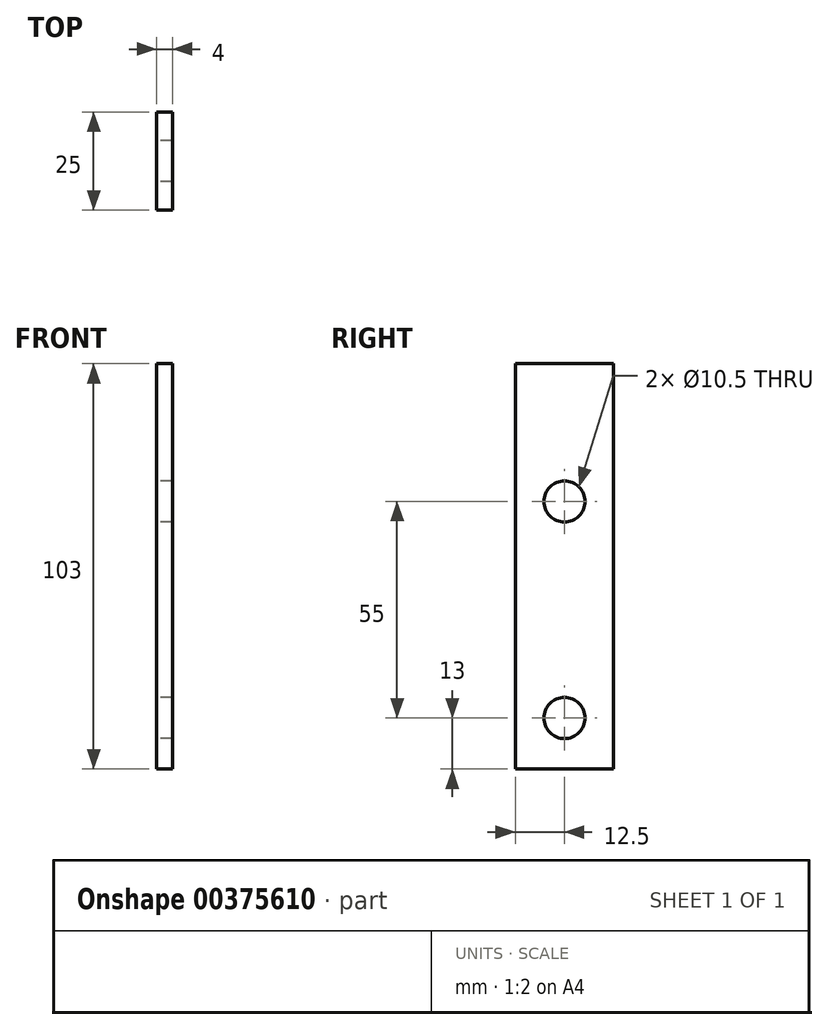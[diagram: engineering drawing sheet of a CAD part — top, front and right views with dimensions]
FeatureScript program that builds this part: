
annotation { "Feature Type Name" : "Feature", "Feature Type Description" : "" }
export const myFeature = defineFeature(function(context is Context, id is Id, definition is map)
    precondition{}
    {
        {
            var Q0;
            Q0=qCreatedBy(makeId("Right.planeOp"),FACE);
            var sketch = newSketch(context, id + "F0", { "sketchPlane" : qUnion([Q0])});
            skLineSegment(sketch, "E0.bottom", {"start": v(12.5, 51.5) * mm, "end": v(-12.5, 51.5) * mm});
            skLineSegment(sketch, "E0.top", {"start": v(12.5, -51.5) * mm, "end": v(-12.5, -51.5) * mm});
            skLineSegment(sketch, "E0.left", {"start": v(12.5, 51.5) * mm, "end": v(12.5, -51.5) * mm});
            skLineSegment(sketch, "E0.right", {"start": v(-12.5, 51.5) * mm, "end": v(-12.5, -51.5) * mm});
            skPoint(sketch, "E0.middle", {"position": v(0, 0) * mm});
            skLineSegment(sketch, "E1.bottom", {"start": v(98.77, -18.5) * mm, "end": v(-98.77, -18.5) * mm, "construction": true});
            skLineSegment(sketch, "E1.top", {"start": v(98.77, -98.5) * mm, "end": v(-98.77, -98.5) * mm, "construction": true});
            skLineSegment(sketch, "E1.left", {"start": v(98.77, -18.5) * mm, "end": v(98.77, -98.5) * mm, "construction": true});
            skLineSegment(sketch, "E1.right", {"start": v(-98.77, -18.5) * mm, "end": v(-98.77, -98.5) * mm, "construction": true});
            skPoint(sketch, "E1.middle", {"position": v(0, -58.5) * mm});
            skCircle(sketch, "E2", {"center": v(0, -38.5) * mm, "radius": 5.25 * mm});
            skCircle(sketch, "E3", {"center": v(0, 16.5) * mm, "radius": 5.25 * mm});
            skSolve(sketch);
        }
        {
            var Q0;
            Q0 = qSketchRegion(id + "F0", true);
            extrude(context, id + "F1", {"entities" : qUnion([Q0]), "depth" : 4 * mm});
        }
    });
